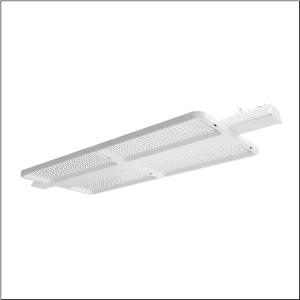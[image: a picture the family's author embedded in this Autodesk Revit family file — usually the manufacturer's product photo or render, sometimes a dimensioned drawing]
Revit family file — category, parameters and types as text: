
# Revit family: highbay_11_fur_licross_r__tragschiene_maxi_51hn12db4vla_45ce
name_source: partatom
category: Lighting Fixtures
units: mm (PartAtom-declared; Revit-internal decimal feet)

## family parameters
Cut with Voids When Loaded = No
Host = Face
Light Source = No
Part Type = Normal
Room Calculation Point = No
Round Connector Dimension = Use Diameter
Shared = No

## types (1)
- --- (1 x LED, 56000 lm, 294.9 W, 4000K)
    Apparent Load = 295 VA
    CIE Flux Codes = 87 98 100 100 100
    Color Rendering = 80
    Color Temperature = 4000K
    Default Elevation = 1800 mm
    Description = high bay luminaire Highbay 11 for Licross® trunking rail maxi; direct symmetric wide distribution, light control with lens of PMMA; UGR ≤ 22 (X = 4H | Y = 8H | S = 0.25H | reflection values 70/50/20); luminous flux: 56.000lm; light colour: 840, colour temperature: 4000K, MacAdam ≤ 2 SDCM (initial), colour rendering: CRI > 80; luminous efficacy: 189,9lm/W; rated service life: 100.000h (L95) at AT= 25°C; control: DALI 2; luminaire connection: plug, 5-pole, with phase selectionmains connection: 230..240V, AC 50/60Hz; connected load: 294,9W; protection rating (complete): IP64; insulation class (complete): insulation class I (protective earthing); protection symbol: D; impact resistance: IK06; certification: CE, ENEC, VDE, UKCA; internal wiring halogen-free; luminaire Suitable for use in the food industry according to the specifications of IFS-Food, HACCP and/or BRC; LABS conformity tested according to VDMA 24364:2018-05; housing frame of high-performance plastic PA6, matt traffic white (RAL 9016); cover of PMMA; fixing on rail side of steel, galvanised, white; blank cover of PC/ABS, traffic white (RAL 9016); dimension (LxWxH): 1.250 x 442 x 71mm; permissible operating ambient temperature: -40..+50°C (reducing of maximum allowable ambient temperature of 5°C with ceiling mounting); packaging unit: 1 piece
    Height = 72 mm  [stored 0.23622 ft]
    Lamp = 1 x LED
    Lamp Light Flux = 56000 lm
    Lamp Power = 294.9 W
    Lamp count = 1
    Length = 946 mm
    Luminous efficacy = 190 lm/W
    Manufacturer = Siteco
    ModVariant = No
    Model = 51HN12DB4VLA
    Mounting Place = Ceiling
    Mounting Type = Pendant
    Number of Poles = 1
    OnlyDefault = Yes
    Power Factor = 1
    Product Name = Highbay 11 für Licross® Tragschiene maxi
    Product group = high bay luminaire
    ProductGroupID = 902
    Protection Class = Protection class I
    Protection Degree = IP 64
    RLX_Detail_Level = 1
    RLX_Emergency_Light_Flux = 0 lm
    RLX_Emergency_Type = 0
    RLX_Emergency_Type_DB = No
    RlxData = <blob elided: 24277 chars, md5=394bfb93>
    Socket = socket
    Standby Power = 0 W
    System Light Flux = 55999 lm
    System Power = 295 W
    Type Comments = factory setting: luminous flux: 100 % | dim-lin: 254 | 664 mA
    Type Image = l_1361711.jpg
    URL = http://relux.com
    VarID = @adj_026663
    Voltage = 0 V
    Weight = 0.00 kg
    Width = 442 mm

note: [stored X ft] marks values corroborated as IEEE doubles in the binary element streams (Revit-internal decimal feet)

## geometry (parser evidence)
native form markers: Blend x4, Sweep x10
no freeform markers — native parametric forms only
